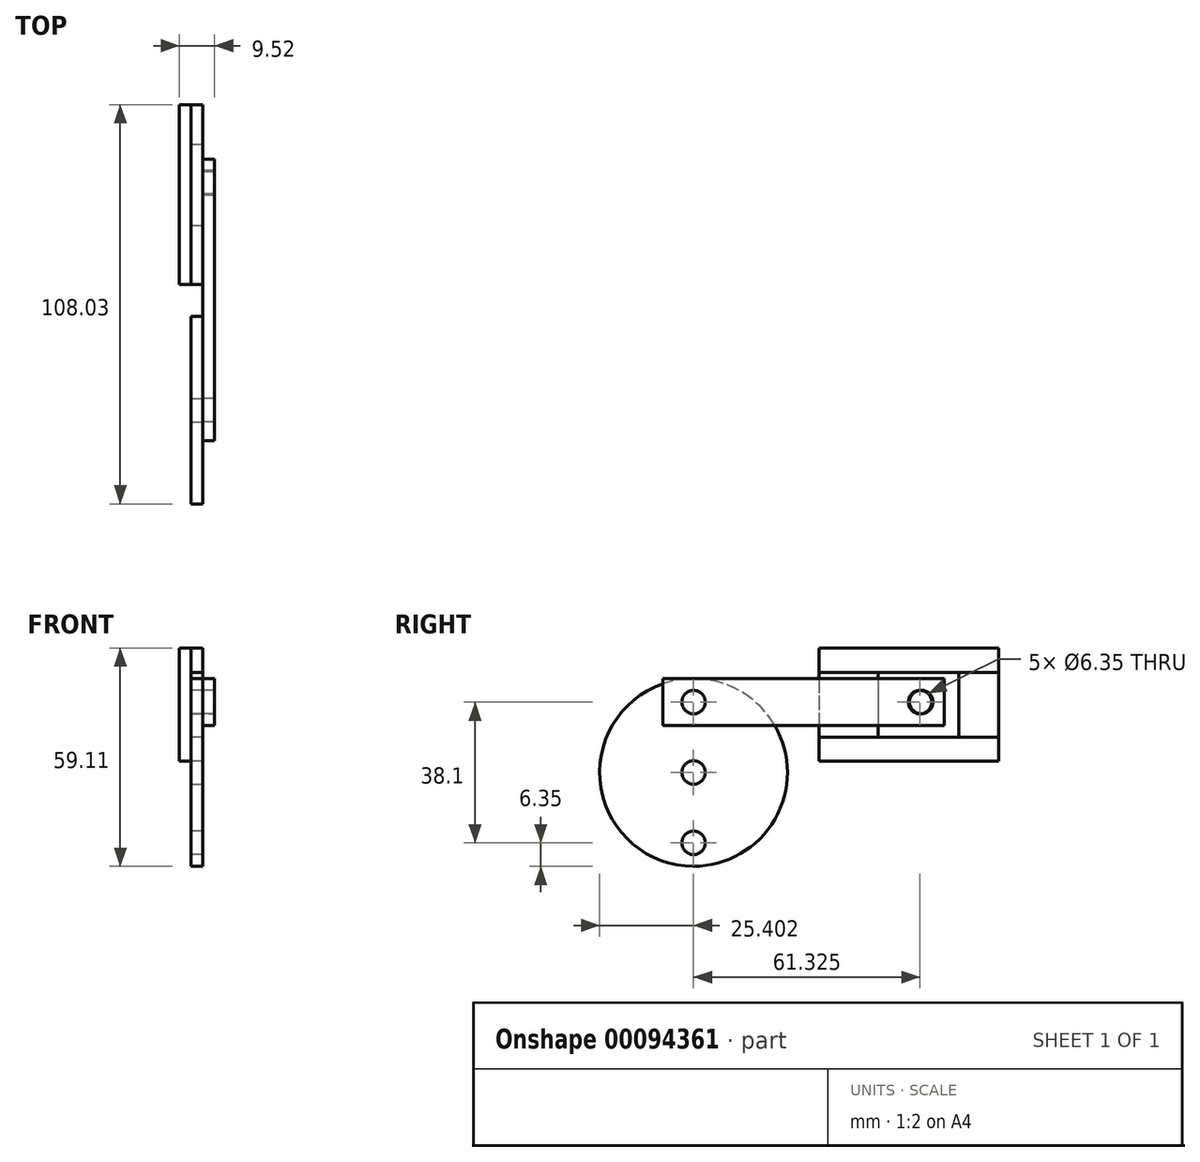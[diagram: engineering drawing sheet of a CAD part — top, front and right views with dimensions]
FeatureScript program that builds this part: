
annotation { "Feature Type Name" : "Feature", "Feature Type Description" : "" }
export const myFeature = defineFeature(function(context is Context, id is Id, definition is map)
    precondition{}
    {
        {
            var Q0;
            Q0=qCreatedBy(makeId("Right.planeOp"),FACE);
            var sketch = newSketch(context, id + "F0", { "sketchPlane" : qUnion([Q0])});
            skCircle(sketch, "E0", {"center": v(-67.86, 0) * mm, "radius": 25.4 * mm});
            skCircle(sketch, "E1", {"center": v(-67.86, 0) * mm, "radius": 3.18 * mm});
            skLineSegment(sketch, "E2", {"start": v(-67.86, 25.4) * mm, "end": v(-67.86, -25.4) * mm, "construction": true});
            skLineSegment(sketch, "E3", {"start": v(-42.46, 0) * mm, "end": v(-93.26, 0) * mm, "construction": true});
            skCircle(sketch, "E4", {"center": v(-67.86, 19.05) * mm, "radius": 3.18 * mm});
            skCircle(sketch, "E5", {"center": v(-67.86, -19.05) * mm, "radius": 3.18 * mm});
            skSolve(sketch);
        }
        {
            var Q0;
            Q0=makeQuery(id+"F0.imprint","IMPRINT",FACE,{"disambiguationData":[TD([[makeQuery(id+"F0.imprint","IMPRINT",EDGE,{"derivedFrom":sQuery(id+"F0.wireOp",EDGE,"E0")}),1.0]])]});
            extrude(context, id + "F1", {"entities" : qUnion([Q0]), "depth" : 3.17 * mm});
        }
        {
            var Q0;
            Q0=makeQuery(id+"F1.opExtrude","CAP_FACE",FACE,{"disambiguationData":[OSD([sQuery(id+"F0.wireOp",EDGE,"E0"),sQuery(id+"F0.wireOp",EDGE,"E1"),sQuery(id+"F0.wireOp",EDGE,"E4"),sQuery(id+"F0.wireOp",EDGE,"E5")])],"isStart":false});
            var sketch = newSketch(context, id + "F2", { "sketchPlane" : qUnion([Q0])});
            skCircle(sketch, "E6", {"center": v(-67.86, 0) * mm, "radius": 3.18 * mm});
            skSolve(sketch);
        }
        {
            var Q0;
            Q0 = qSketchRegion(id + "F2", true);
            extrude(context, id + "F3", {"entities" : qUnion([Q0]), "oppositeDirection" : true, "depth" : 3.17 * mm});
        }
        {
            var Q0;
            Q0=makeQuery(id+"F1.opExtrude","CAP_FACE",FACE,{"disambiguationData":[OSD([sQuery(id+"F0.wireOp",EDGE,"E0"),sQuery(id+"F0.wireOp",EDGE,"E1"),sQuery(id+"F0.wireOp",EDGE,"E4"),sQuery(id+"F0.wireOp",EDGE,"E5")])],"isStart":false});
            var sketch = newSketch(context, id + "F4", { "sketchPlane" : qUnion([Q0])});
            skLineSegment(sketch, "E7.bottom", {"start": v(0, 25.4) * mm, "end": v(-76.2, 25.4) * mm});
            skLineSegment(sketch, "E7.top", {"start": v(0, 12.7) * mm, "end": v(-76.2, 12.7) * mm});
            skLineSegment(sketch, "E7.left", {"start": v(0, 25.4) * mm, "end": v(0, 12.7) * mm});
            skLineSegment(sketch, "E7.right", {"start": v(-76.2, 25.4) * mm, "end": v(-76.2, 12.7) * mm});
            skCircle(sketch, "E8", {"center": v(-67.86, 19.05) * mm, "radius": 3.18 * mm});
            skCircle(sketch, "E9", {"center": v(-6.53, 19.05) * mm, "radius": 3.18 * mm});
            skPoint(sketch, "E9.centerSnap0", {"position": v(0, 19.05) * mm});
            skSolve(sketch);
        }
        {
            var Q0;
            Q0 = qSketchRegion(id + "F4", true);
            extrude(context, id + "F5", {"entities" : qUnion([Q0]), "depth" : 3.17 * mm});
        }
        {
            var Q0;
            Q0=makeQuery(id+"F5.opExtrude","CAP_FACE",FACE,{"disambiguationData":[OSD([sQuery(id+"F4.wireOp",EDGE,"E7.bottom"),sQuery(id+"F4.wireOp",EDGE,"E7.top"),sQuery(id+"F4.wireOp",EDGE,"E7.left"),sQuery(id+"F4.wireOp",EDGE,"E7.right"),sQuery(id+"F4.wireOp",EDGE,"E8")])],"isStart":true});
            var sketch = newSketch(context, id + "F6", { "sketchPlane" : qUnion([Q0])});
            skCircle(sketch, "E10", {"center": v(67.86, 19.05) * mm, "radius": 3.18 * mm});
            skSolve(sketch);
        }
        {
            var Q0;
            Q0 = qSketchRegion(id + "F6", true);
            extrude(context, id + "F7", {"entities" : qUnion([Q0]), "depth" : 3.17 * mm, "hasSecondDirection" : true, "secondDirectionOppositeDirection" : true, "secondDirectionDepth" : 3.17 * mm});
        }
        {
            var Q0;
            Q0=qCreatedBy(makeId("Right.planeOp"),FACE);
            var sketch = newSketch(context, id + "F8", { "sketchPlane" : qUnion([Q0])});
            skCircle(sketch, "E11", {"center": v(-6.2, 19.1) * mm, "radius": 3.18 * mm});
            skLineSegment(sketch, "E12.bottom", {"start": v(3.98, 27.04) * mm, "end": v(-17.94, 27.04) * mm});
            skLineSegment(sketch, "E12.top", {"start": v(3.98, 9.52) * mm, "end": v(-17.94, 9.52) * mm});
            skLineSegment(sketch, "E12.left", {"start": v(3.98, 27.04) * mm, "end": v(3.98, 9.52) * mm});
            skLineSegment(sketch, "E12.right", {"start": v(-17.94, 27.04) * mm, "end": v(-17.94, 9.52) * mm});
            skSolve(sketch);
        }
        {
            var Q0;
            Q0=makeQuery(id+"F8.imprint","IMPRINT",FACE,{"disambiguationData":[TD([[makeQuery(id+"F8.imprint","IMPRINT",EDGE,{"derivedFrom":sQuery(id+"F8.wireOp",EDGE,"E11")}),-1.0]])]});
            extrude(context, id + "F9", {"entities" : qUnion([Q0]), "depth" : 3.17 * mm});
        }
        {
            var Q0;
            Q0=makeQuery(id+"F9.opExtrude","CAP_FACE",FACE,{"disambiguationData":[OSD([sQuery(id+"F8.wireOp",EDGE,"E11"),sQuery(id+"F8.wireOp",EDGE,"E12.bottom"),sQuery(id+"F8.wireOp",EDGE,"E12.top"),sQuery(id+"F8.wireOp",EDGE,"E12.left"),sQuery(id+"F8.wireOp",EDGE,"E12.right")])],"isStart":true});
            var sketch = newSketch(context, id + "F10", { "sketchPlane" : qUnion([Q0])});
            skCircle(sketch, "E13", {"center": v(6.2, 19.1) * mm, "radius": 3.17 * mm});
            skSolve(sketch);
        }
        {
            var Q0;
            Q0 = qSketchRegion(id + "F10", true);
            extrude(context, id + "F11", {"entities" : qUnion([Q0]), "oppositeDirection" : true, "depth" : 6.35 * mm});
        }
        {
            var Q0;
            Q0=makeQuery(id+"F9.opExtrude","SWEPT_BODY",BODY,{"disambiguationData":[OSD([sQuery(id+"F8.wireOp",EDGE,"E11"),sQuery(id+"F8.wireOp",EDGE,"E12.bottom"),sQuery(id+"F8.wireOp",EDGE,"E12.top"),sQuery(id+"F8.wireOp",EDGE,"E12.left"),sQuery(id+"F8.wireOp",EDGE,"E12.right")])]});
            var Q1;
            Q1=makeQuery(id+"F11.opExtrude","SWEPT_BODY",BODY,{"disambiguationData":[OSD([sQuery(id+"F10.wireOp",EDGE,"E13")])]});
            booleanBodies(context, id + "F12", {"operationType" : BooleanOperationType.UNION, "tools" : qUnion([Q0, Q1])});
        }
        {
            var Q0;
            Q0=makeQuery(id+"F12.opBoolean","MERGE",FACE,{"derivedFrom":[makeQuery(id+"F9.opExtrude","CAP_FACE",FACE,{"disambiguationData":[OSD([sQuery(id+"F8.wireOp",EDGE,"E11"),sQuery(id+"F8.wireOp",EDGE,"E12.bottom"),sQuery(id+"F8.wireOp",EDGE,"E12.top"),sQuery(id+"F8.wireOp",EDGE,"E12.left"),sQuery(id+"F8.wireOp",EDGE,"E12.right")])],"isStart":true}),makeQuery(id+"F11.opExtrude","CAP_FACE",FACE,{"disambiguationData":[OSD([sQuery(id+"F10.wireOp",EDGE,"E13")])],"isStart":true})]});
            var sketch = newSketch(context, id + "F13", { "sketchPlane" : qUnion([Q0])});
            skLineSegment(sketch, "E14.bottom", {"start": v(-14.77, 33.7) * mm, "end": v(33.9, 33.7) * mm});
            skLineSegment(sketch, "E14.top", {"start": v(-14.77, 3.1) * mm, "end": v(33.9, 3.1) * mm});
            skLineSegment(sketch, "E14.left", {"start": v(-14.77, 33.7) * mm, "end": v(-14.77, 3.1) * mm});
            skLineSegment(sketch, "E14.right", {"start": v(33.9, 33.7) * mm, "end": v(33.9, 3.1) * mm});
            skLineSegment(sketch, "E15.bottom", {"start": v(-14.77, 27.04) * mm, "end": v(33.9, 27.04) * mm});
            skLineSegment(sketch, "E15.top", {"start": v(-14.77, 9.52) * mm, "end": v(33.9, 9.52) * mm});
            skLineSegment(sketch, "E15.left", {"start": v(-14.77, 27.04) * mm, "end": v(-14.77, 9.52) * mm});
            skLineSegment(sketch, "E15.right", {"start": v(33.9, 27.04) * mm, "end": v(33.9, 9.52) * mm});
            skSolve(sketch);
        }
        {
            var Q0;
            Q0 = qSketchRegion(id + "F13", true);
            extrude(context, id + "F14", {"entities" : qUnion([Q0]), "depth" : 3.17 * mm});
        }
        {
            var Q0;
            {var subQ4=sQuery(id+"F13.wireOp",EDGE,"E14.bottom");Q0=makeQuery(id+"F13.imprint","IMPRINT",FACE,{"disambiguationData":[TD([[makeQuery(id+"F13.imprint","IMPRINT",EDGE,{"derivedFrom":subQ4}),-1.0]])]});}
            var Q1;
            {var subQ4=sQuery(id+"F13.wireOp",EDGE,"E14.top");Q1=makeQuery(id+"F13.imprint","IMPRINT",FACE,{"disambiguationData":[TD([[makeQuery(id+"F13.imprint","IMPRINT",EDGE,{"derivedFrom":subQ4}),1.0]])]});}
            extrude(context, id + "F15", {"entities" : qUnion([Q0, Q1]), "oppositeDirection" : true, "depth" : 3.17 * mm});
        }
    });
